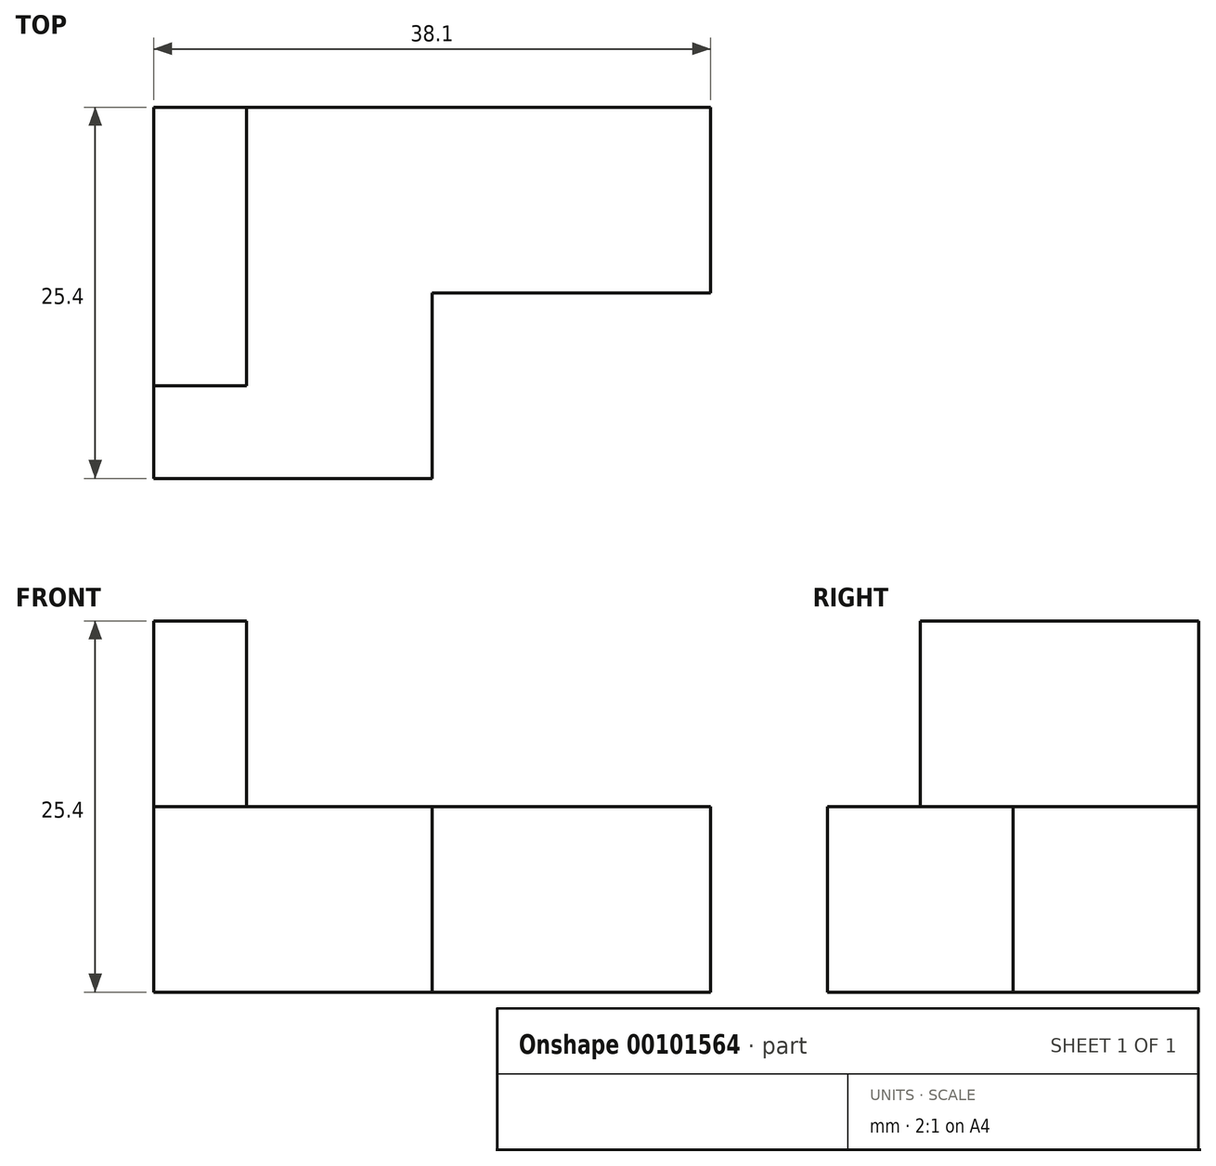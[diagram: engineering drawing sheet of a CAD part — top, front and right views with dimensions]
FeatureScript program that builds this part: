
annotation { "Feature Type Name" : "Feature", "Feature Type Description" : "" }
export const myFeature = defineFeature(function(context is Context, id is Id, definition is map)
    precondition{}
    {
        {
            var Q0;
            Q0=qCreatedBy(makeId("Front.planeOp"),FACE);
            var sketch = newSketch(context, id + "F0", { "sketchPlane" : qUnion([Q0])});
            skLineSegment(sketch, "E0", {"start": v(0, 0) * mm, "end": v(0, -12.7) * mm});
            skLineSegment(sketch, "E1", {"start": v(0, -12.7) * mm, "end": v(6.35, -12.7) * mm});
            skLineSegment(sketch, "E2", {"start": v(6.35, -12.7) * mm, "end": v(6.35, 0) * mm});
            skLineSegment(sketch, "E3", {"start": v(6.35, 0) * mm, "end": v(0, 0) * mm});
            skLineSegment(sketch, "E4", {"start": v(0, -12.7) * mm, "end": v(38.1, -12.7) * mm});
            skLineSegment(sketch, "E5", {"start": v(38.1, -12.7) * mm, "end": v(38.1, -25.4) * mm});
            skLineSegment(sketch, "E6", {"start": v(0, -25.4) * mm, "end": v(0, -12.7) * mm});
            skLineSegment(sketch, "E7", {"start": v(0, -25.4) * mm, "end": v(38.1, -25.4) * mm});
            skSolve(sketch);
        }
        {
            var Q0;
            {var subQ1=sQuery(id+"F0.wireOp",EDGE,"E5");Q0=makeQuery(id+"F0.imprint","IMPRINT",FACE,{"disambiguationData":[TD([[makeQuery(id+"F0.imprint","IMPRINT",EDGE,{"derivedFrom":subQ1}),-1.0]])]});}
            var Q1;
            {var subQ0=sQuery(id+"F0.wireOp",EDGE,"E0");Q1=makeQuery(id+"F0.imprint","IMPRINT",FACE,{"disambiguationData":[TD([[makeQuery(id+"F0.imprint","IMPRINT",EDGE,{"derivedFrom":subQ0}),1.0]])]});}
            extrude(context, id + "F1", {"entities" : qUnion([Q0, Q1]), "depth" : 25.4 * mm});
        }
        {
            var Q0;
            Q0=qCreatedBy(makeId("Top.planeOp"),FACE);
            var sketch = newSketch(context, id + "F2", { "sketchPlane" : qUnion([Q0])});
            skLineSegment(sketch, "E8.bottom", {"start": v(0, -25.4) * mm, "end": v(6.35, -25.4) * mm});
            skLineSegment(sketch, "E8.top", {"start": v(0, -19.05) * mm, "end": v(6.35, -19.05) * mm});
            skLineSegment(sketch, "E8.left", {"start": v(0, -25.4) * mm, "end": v(0, -19.05) * mm});
            skLineSegment(sketch, "E8.right", {"start": v(6.35, -25.4) * mm, "end": v(6.35, -19.05) * mm});
            skSolve(sketch);
        }
        {
            var Q0;
            Q0 = qSketchRegion(id + "F2", true);
            extrude(context, id + "F3", {"entities" : qUnion([Q0]), "operationType" : NewBodyOperationType.REMOVE, "oppositeDirection" : true, "depth" : 12.7 * mm});
        }
        {
            var Q0;
            Q0=qCreatedBy(makeId("Top.planeOp"),FACE);
            var sketch = newSketch(context, id + "F4", { "sketchPlane" : qUnion([Q0])});
            skLineSegment(sketch, "E9.bottom", {"start": v(38.1, -25.4) * mm, "end": v(19.05, -25.4) * mm});
            skLineSegment(sketch, "E9.top", {"start": v(38.1, -12.7) * mm, "end": v(19.05, -12.7) * mm});
            skLineSegment(sketch, "E9.left", {"start": v(38.1, -25.4) * mm, "end": v(38.1, -12.7) * mm});
            skLineSegment(sketch, "E9.right", {"start": v(19.05, -25.4) * mm, "end": v(19.05, -12.7) * mm});
            skSolve(sketch);
        }
        {
            var Q0;
            Q0 = qSketchRegion(id + "F4", true);
            extrude(context, id + "F5", {"entities" : qUnion([Q0]), "operationType" : NewBodyOperationType.REMOVE, "endBound" : BoundingType.THROUGH_ALL, "oppositeDirection" : true, "depth" : 25.4 * mm});
        }
    });
